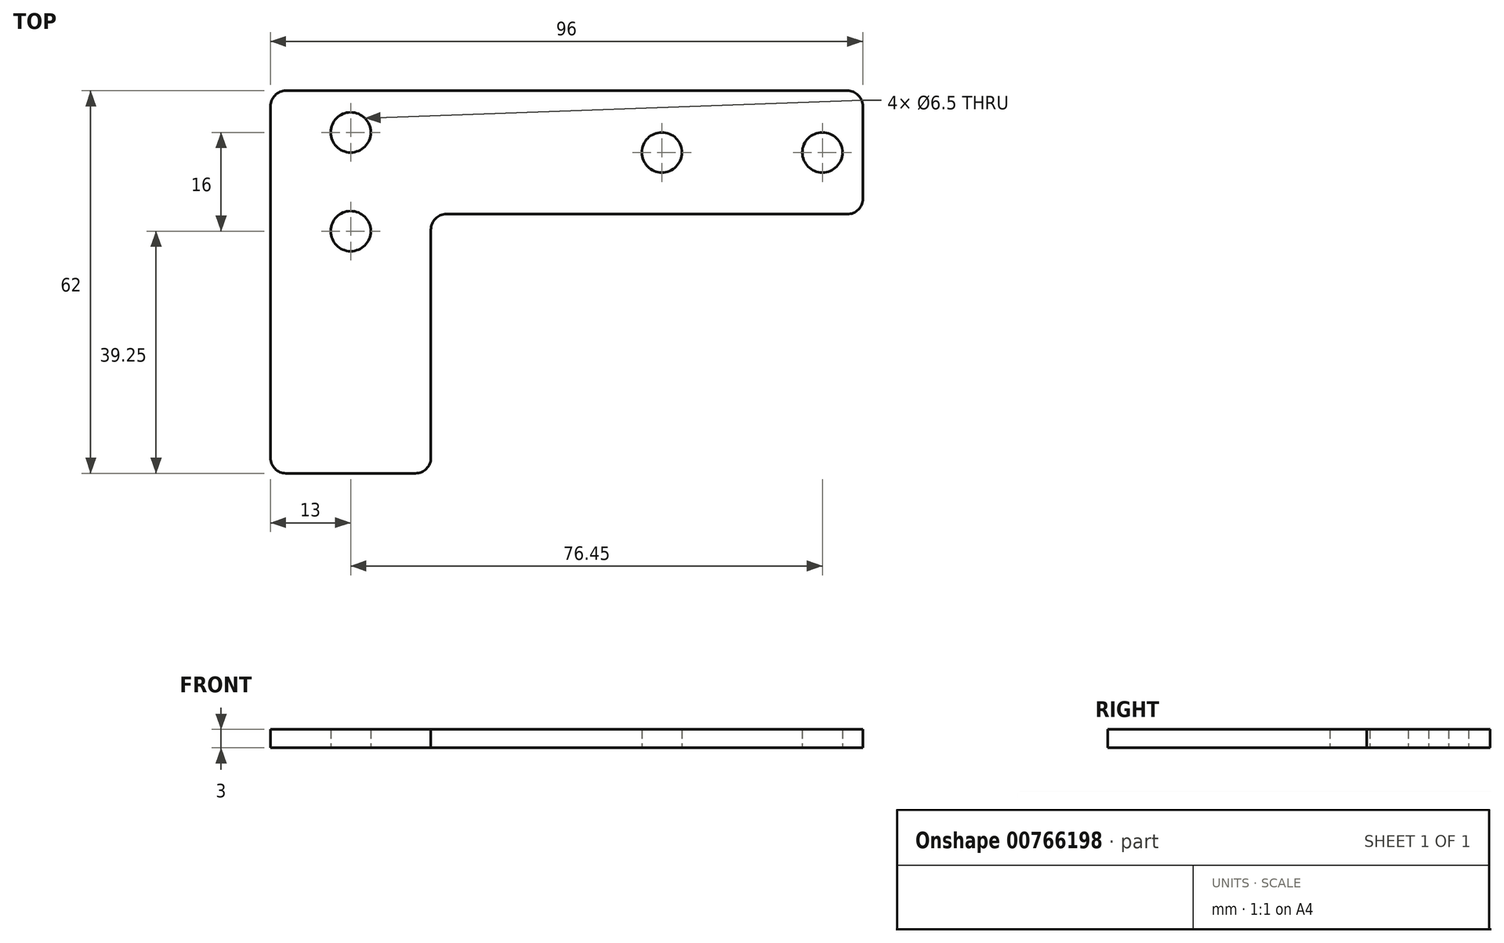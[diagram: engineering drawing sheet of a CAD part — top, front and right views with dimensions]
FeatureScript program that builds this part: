
annotation { "Feature Type Name" : "Feature", "Feature Type Description" : "" }
export const myFeature = defineFeature(function(context is Context, id is Id, definition is map)
    precondition{}
    {
        {
            var Q0;
            Q0=qCreatedBy(makeId("Top.planeOp"),FACE);
            var sketch = newSketch(context, id + "F0", { "sketchPlane" : qUnion([Q0])});
            skLineSegment(sketch, "E0.bottom", {"start": v(13, 10) * mm, "end": v(80.5, 10) * mm});
            skLineSegment(sketch, "E0.top", {"start": v(15.5, -10) * mm, "end": v(80.5, -10) * mm});
            skLineSegment(sketch, "E0.left", {"start": v(13, 10) * mm, "end": v(13, -10) * mm});
            skLineSegment(sketch, "E0.right", {"start": v(83, 7.5) * mm, "end": v(83, -7.5) * mm});
            skLineSegment(sketch, "E1.bottom", {"start": v(13, 10) * mm, "end": v(-10.5, 10) * mm});
            skLineSegment(sketch, "E1.top", {"start": v(10.5, -52) * mm, "end": v(-10.5, -52) * mm});
            skLineSegment(sketch, "E1.left", {"start": v(13, -12.5) * mm, "end": v(13, -49.5) * mm});
            skLineSegment(sketch, "E1.right", {"start": v(-13, 7.5) * mm, "end": v(-13, -49.5) * mm});
            skCircle(sketch, "E2", {"center": v(0, 3.25) * mm, "radius": 3.25 * mm});
            skCircle(sketch, "E3", {"center": v(0, -12.75) * mm, "radius": 3.25 * mm});
            skCircle(sketch, "E4", {"center": v(76.45, 0) * mm, "radius": 3.25 * mm});
            skPoint(sketch, "E5.visualSharp", {"position": v(-13, -52) * mm});
            skArc(sketch, "E5.filletArc", {"start": v(-13, -49.5) * mm, "mid": v(-12.27, -51.27) * mm, "end": v(-10.5, -52) * mm});
            skPoint(sketch, "E6.visualSharp", {"position": v(13, -52) * mm});
            skArc(sketch, "E6.filletArc", {"start": v(10.5, -52) * mm, "mid": v(12.27, -51.27) * mm, "end": v(13, -49.5) * mm});
            skPoint(sketch, "E7.visualSharp", {"position": v(-13, 10) * mm});
            skArc(sketch, "E7.filletArc", {"start": v(-10.5, 10) * mm, "mid": v(-12.27, 9.27) * mm, "end": v(-13, 7.5) * mm});
            skPoint(sketch, "E8.visualSharp", {"position": v(83, 10) * mm});
            skArc(sketch, "E8.filletArc", {"start": v(83, 7.5) * mm, "mid": v(82.27, 9.27) * mm, "end": v(80.5, 10) * mm});
            skPoint(sketch, "E9.visualSharp", {"position": v(83, -10) * mm});
            skArc(sketch, "E9.filletArc", {"start": v(80.5, -10) * mm, "mid": v(82.27, -9.27) * mm, "end": v(83, -7.5) * mm});
            skArc(sketch, "E10.filletArc", {"start": v(15.5, -10) * mm, "mid": v(13.73, -10.73) * mm, "end": v(13, -12.5) * mm});
            skCircle(sketch, "E11", {"center": v(50.44, 0) * mm, "radius": 3.25 * mm});
            skSolve(sketch);
        }
        {
            var Q0;
            Q0=makeQuery(id+"F0.imprint","IMPRINT",FACE,{"disambiguationData":[TD([[makeQuery(id+"F0.imprint","IMPRINT",EDGE,{"derivedFrom":sQuery(id+"F0.wireOp",EDGE,"E0.bottom")}),-1.0]])]});
            extrude(context, id + "F1", {"entities" : qUnion([Q0]), "depth" : 3 * mm, "offsetDistance" : 25 * mm});
        }
    });
